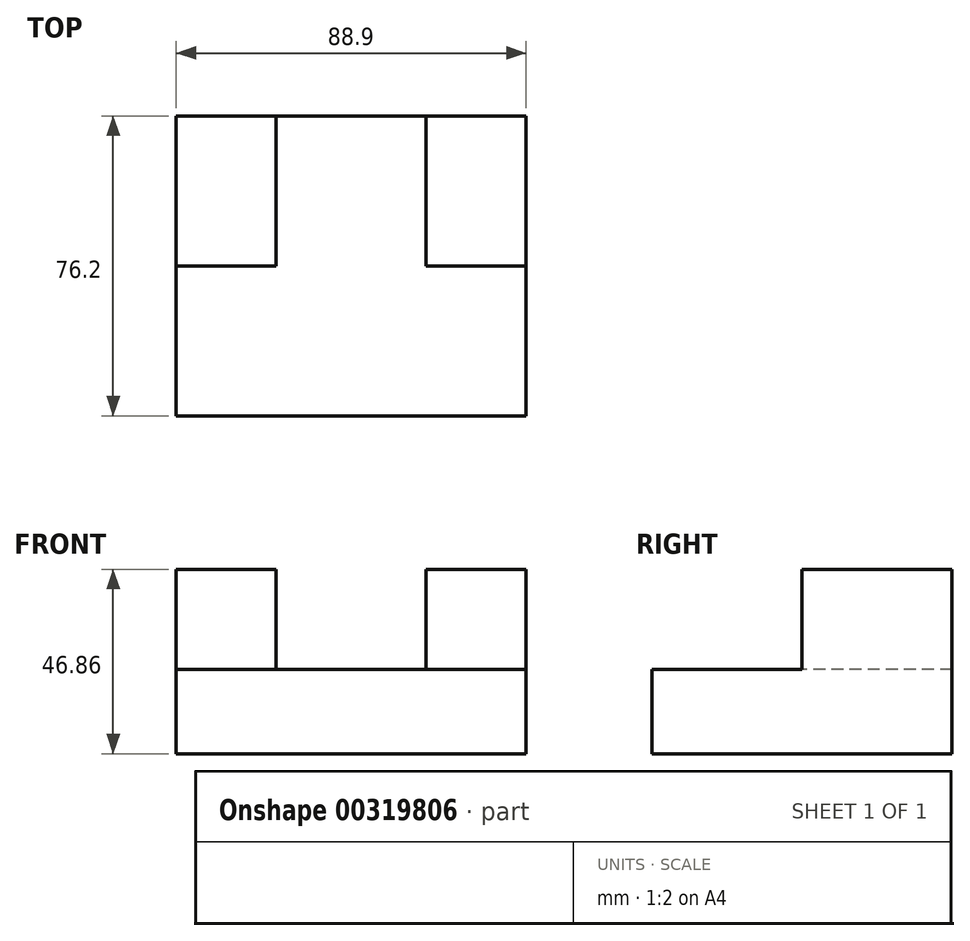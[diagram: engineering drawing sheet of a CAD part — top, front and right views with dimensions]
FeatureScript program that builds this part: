
annotation { "Feature Type Name" : "Feature", "Feature Type Description" : "" }
export const myFeature = defineFeature(function(context is Context, id is Id, definition is map)
    precondition{}
    {
        {
            var Q0;
            Q0=qCreatedBy(makeId("Front.planeOp"),FACE);
            var sketch = newSketch(context, id + "F0", { "sketchPlane" : qUnion([Q0])});
            skLineSegment(sketch, "E0.bottom", {"start": v(-41.5, -27.87) * mm, "end": v(47.4, -27.87) * mm});
            skLineSegment(sketch, "E0.top", {"start": v(-41.5, -49.33) * mm, "end": v(47.4, -49.33) * mm});
            skLineSegment(sketch, "E0.left", {"start": v(-41.5, -27.87) * mm, "end": v(-41.5, -49.33) * mm});
            skLineSegment(sketch, "E0.right", {"start": v(47.4, -27.87) * mm, "end": v(47.4, -49.33) * mm});
            skSolve(sketch);
        }
        {
            var Q0;
            Q0 = qSketchRegion(id + "F0", true);
            extrude(context, id + "F1", {"entities" : qUnion([Q0]), "depth" : 76.2 * mm});
        }
        {
            var Q0;
            Q0=makeQuery(id+"F1.opExtrude","SWEPT_FACE",FACE,{"disambiguationData":[OSD([sQuery(id+"F0.wireOp",EDGE,"E0.bottom")])]});
            var sketch = newSketch(context, id + "F2", { "sketchPlane" : qUnion([Q0])});
            skLineSegment(sketch, "E1.bottom", {"start": v(-41.5, 0) * mm, "end": v(-16.1, 0) * mm});
            skLineSegment(sketch, "E1.top", {"start": v(-41.5, -38.1) * mm, "end": v(-16.1, -38.1) * mm});
            skLineSegment(sketch, "E1.left", {"start": v(-41.5, 0) * mm, "end": v(-41.5, -38.1) * mm});
            skLineSegment(sketch, "E1.right", {"start": v(-16.1, 0) * mm, "end": v(-16.1, -38.1) * mm});
            skLineSegment(sketch, "E2.bottom", {"start": v(22, 0) * mm, "end": v(47.4, 0) * mm});
            skLineSegment(sketch, "E2.top", {"start": v(22, -38.1) * mm, "end": v(47.4, -38.1) * mm});
            skLineSegment(sketch, "E2.left", {"start": v(22, 0) * mm, "end": v(22, -38.1) * mm});
            skLineSegment(sketch, "E2.right", {"start": v(47.4, 0) * mm, "end": v(47.4, -38.1) * mm});
            skSolve(sketch);
        }
        {
            var Q0;
            Q0=makeQuery(id+"F2.imprint","IMPRINT",FACE,{"disambiguationData":[TD([[makeQuery(id+"F2.imprint","IMPRINT",EDGE,{"derivedFrom":sQuery(id+"F2.wireOp",EDGE,"E1.bottom")}),-1.0]])]});
            extrude(context, id + "F3", {"entities" : qUnion([Q0]), "operationType" : NewBodyOperationType.ADD, "depth" : 25.4 * mm});
        }
        {
            var Q0;
            Q0=makeQuery(id+"F1.opExtrude","SWEPT_FACE",FACE,{"disambiguationData":[OSD([sQuery(id+"F0.wireOp",EDGE,"E0.bottom")])]});
            var sketch = newSketch(context, id + "F4", { "sketchPlane" : qUnion([Q0])});
            skLineSegment(sketch, "E3", {"start": v(22, 0) * mm, "end": v(22, -38.1) * mm});
            skLineSegment(sketch, "E4", {"start": v(22, -38.1) * mm, "end": v(47.4, -38.1) * mm});
            skLineSegment(sketch, "E5", {"start": v(47.4, 0) * mm, "end": v(47.4, -38.1) * mm});
            skLineSegment(sketch, "E6", {"start": v(22, 0) * mm, "end": v(47.4, 0) * mm});
            skSolve(sketch);
        }
        {
            var Q0;
            Q0 = qSketchRegion(id + "F4", true);
            extrude(context, id + "F5", {"entities" : qUnion([Q0]), "operationType" : NewBodyOperationType.ADD, "depth" : 25.4 * mm});
        }
    });
